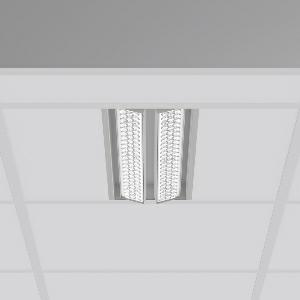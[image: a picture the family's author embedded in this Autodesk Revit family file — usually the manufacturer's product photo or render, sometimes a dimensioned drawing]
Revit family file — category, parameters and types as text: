
# Revit family: tx-move_901733_004_aeea
name_source: partatom
category: Lighting Fixtures
units: mm (PartAtom-declared; Revit-internal decimal feet)

## family parameters
Cut with Voids When Loaded = No
Host = Face
Light Source = No
Part Type = Normal
Room Calculation Point = No
Round Connector Dimension = Use Diameter
Shared = No

## types (1)
- MultiLumen 1 (1 x LED Modul 830, 2800 lm, 3000)
    Apparent Load = 35 VA
    Approval mark = CE
    CIE Flux Codes = 77 96 99 100 100
    Color Rendering = 80
    Color Temperature = 3000
    Default Elevation = 1800 mm
    Description = Series: TX-MOVE
Einlege/Einbau-Flächenstrahler. Housing: sheet steel, powder-coated. 2xSwivel range: 90°. High-efficiency LED units with optimum light control thanks to clear plastic (PC) lens optics. Spezielle Mikrostrukturen reduzieren Gelbsaum. Symmetrical light distribution. Suitable for laying in grid ceiling module 600. Connected converter included in separate gearbox.Suitable for through-wiring.MultiLumen: Luminous flux adjustable in 3 steps. Accessories: Mounting frame for installation in suspended ceilings. Environmentally friendly and resource-saving due to replaceable and recyclable components. 
Colour: silver, matt (approx. RAL 9006)
Length: 597 mm
Width: 190 mm
Height: 39 mm
Cut-out length: 577.5 mm
Cut-out width: 174 mm
Recess height: 100 mm
Lamp: LED
Socket: without socket
Colour temperature: 3000K
Colour rendering index (CRI): 80
System power: 35 W
Rated luminous flux: 5600 lm
Luminous efficiency: 160 lm/W
System power 2: 47 W
Rated luminous flux 2: 7250 lm
Luminous efficiency 2: 154 lm/W
System power 3: 68 W
Rated luminous flux 3: 9850 lm
Luminous efficiency 3: 145 lm/W
Control gear: Regulated power supply
Protection class: I
Type of protection: IP 20
    Height = 0 mm  [stored 0 ft]
    Lamp = 1 x LED Modul 830
    Lamp Light Flux = 2800 lm
    Lamp count = 1
    Length = 597 mm
    Lifetime = 50000 h
    Luminous efficacy = 160 lm/W
    Manufacturer = RZB
    ModVariant = No
    Model = 901733.004
    Mounting Place = Ceiling, Wall
    Mounting Type = Recessed
    Number of Poles = 1
    OnlyDefault = Yes
    Power Factor = 1
    Product Name = TX-MOVE
    Product group = Recessed projectors
    ProductGroupID = 401
    Protection Class = Protection class I
    Protection Degree = IP 20
    RLX_Detail_Level = 1
    RLX_Emergency_Light_Flux = 0 lm
    RLX_Emergency_Type = 0
    RLX_Emergency_Type_DB = No
    RlxData = <blob elided: 35509 chars, md5=584bd958>
    Socket = socket
    Standby Power = 0 W
    System Light Flux = 5600 lm
    System Power = 35 W
    Type Comments = MultiLumen 1
    Type Image = 901733.004.jpg
    URL = http://relux.com
    VarID = multilumen_1
    Voltage = 230 V
    Voltage Range = 220-240 V
    Weight = 0.00 kg
    Width = 190 mm  [stored 0.62336 ft]

note: [stored X ft] marks values corroborated as IEEE doubles in the binary element streams (Revit-internal decimal feet)

## geometry (parser evidence)
native form markers: Blend x4, Sweep x13
no freeform markers — native parametric forms only
